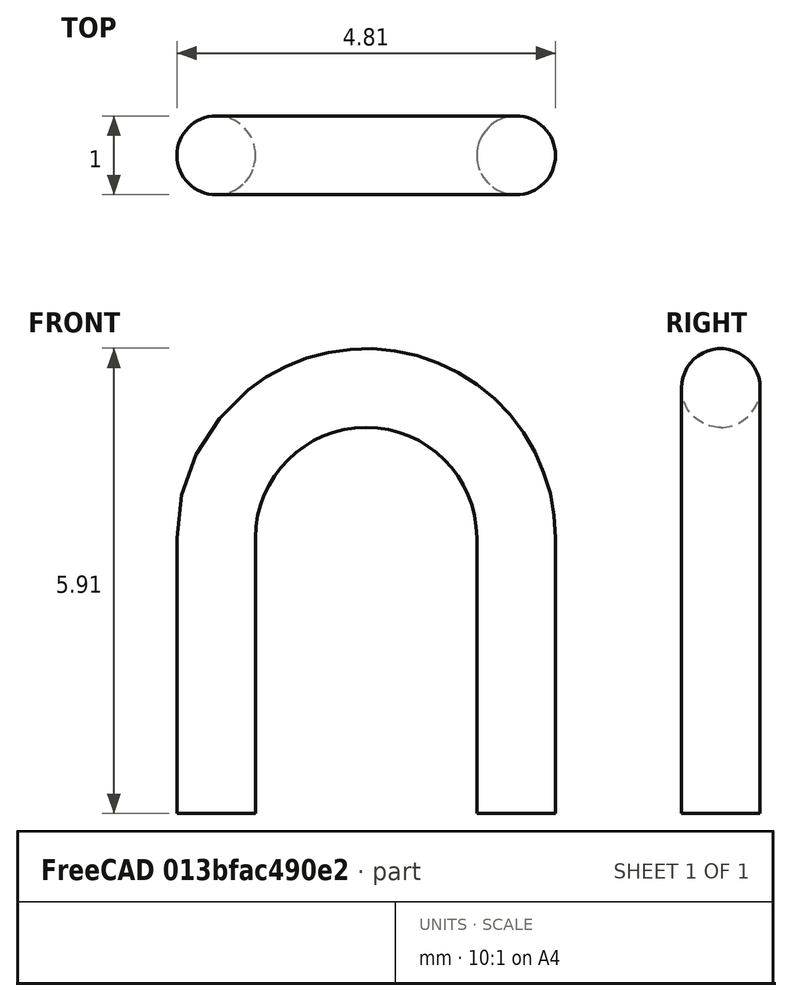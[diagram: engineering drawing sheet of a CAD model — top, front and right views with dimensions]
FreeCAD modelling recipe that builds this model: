
FCSTD DOCUMENT  (FreeCAD 0.17R12018 (Git))
Label: Test_Point_Bridge_Pitch3.81mm_Drill1.3mm
License: All rights reserved
LicenseURL: http://en.wikipedia.org/wiki/All_rights_reserved
objects: Sketcher::SketchObject×2, Spreadsheet::Sheet×1, PartDesign::SubtractivePipe×1, PartDesign::Body×1
note: 5 computed .brp shape members not serialized (recipe doc carries the construction recipe); baked Part::Feature solids carry a one-line shape summary decoded from their .brp

FEATURE [Sketcher::SketchObject] Sketch
  MapMode = 5
  Placement = pos=(0,0,-3) rot=(0,0,1;0rad)
  Support = -> [XY_Plane]
  superPlacement = pos=(0,0,-3) rot=(0,0,1;0rad)
  expr: Constraints[1] = dims.DWire / 2
  sketch-geometry (1):
    g0: Circle CenterX=0 CenterY=0 CenterZ=0 NormalX=0 NormalY=0 NormalZ=1 Radius=0.5
  constraints (2):
    c: Coincident(g0,g-1)
    c: Radius(g0) = 0.5
FEATURE [Spreadsheet::Sheet] Spreadsheet  label="dims"
  cells = A1="DWire"; B1(DWire)=1; A2="Pitch"; B2(Pitch)=3.8100000000000001
FEATURE [Sketcher::SketchObject] Sketch001
  MapMode = 5
  Placement = pos=(0,0,0) rot=(1,0,0;1.5708rad)
  Support = -> [XZ_Plane]
  expr: Constraints[10] = dims.DWire / 2
  expr: Constraints[3] = dims.Pitch
  sketch-geometry (4):
    g0: LineSegment StartX=0 StartY=-3 StartZ=0 EndX=0 EndY=0.5 EndZ=0
    g1: LineSegment StartX=3.81 StartY=0.5 StartZ=0 EndX=3.81 EndY=-3 EndZ=0
    g2: LineSegment [constr] StartX=0 StartY=0.5 StartZ=0 EndX=3.81 EndY=0.5 EndZ=0
    g3: ArcOfCircle CenterX=1.905 CenterY=0.5 CenterZ=0 NormalX=0 NormalY=0 NormalZ=1 Radius=1.905 StartAngle=0 EndAngle=3.14159
  constraints (13):
    c: PointOnObject(g0,g-2)
    c: Vertical(g0)
    c: Vertical(g1)
    c: DistanceX(g0,g1) = 3.81
    c: Coincident(g2,g0)
    c: Coincident(g2,g1)
    c: Horizontal(g2)
    c: PointOnObject(g3,g2)
    c: Coincident(g3,g0)
    c: Coincident(g3,g1)
    c: DistanceY(g-1,g3) = 0.5
    c: DistanceY(g0,g-1) = 3
    c: Equal(g1,g0)
FEATURE [PartDesign::SubtractivePipe] SubtractivePipe
  AuxilleryCurvelinear = true
  AuxillerySpineTangent = false
  Binormal = (0,0,0)
  Mode = 0
  Profile = -> Sketch
  Spine = -> Sketch001
  SpineTangent = false
  Transformation = 0
  Transition = 0
FEATURE [PartDesign::Body] Body  label="Test_Point_Bridge_Pitch3.81mm_Drill1.3mm"
  Group = -> [Sketch,Sketch001,SubtractivePipe]
  Origin = -> Origin
  Tip = -> SubtractivePipe
